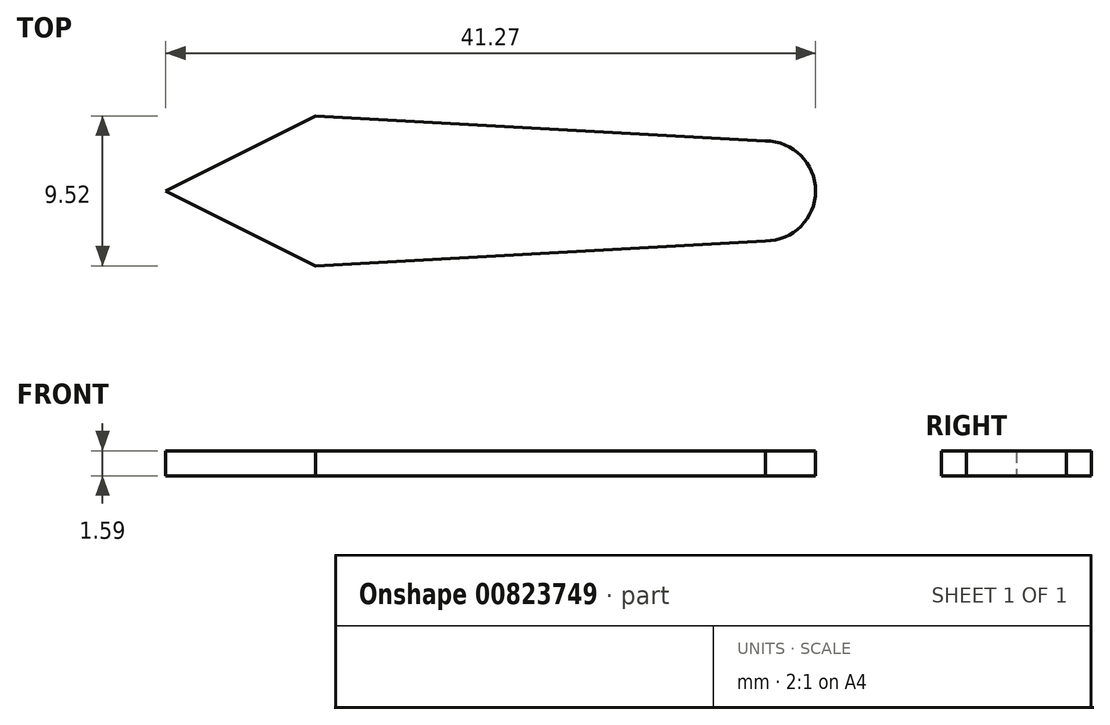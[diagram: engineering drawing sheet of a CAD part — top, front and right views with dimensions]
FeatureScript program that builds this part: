
annotation { "Feature Type Name" : "Feature", "Feature Type Description" : "" }
export const myFeature = defineFeature(function(context is Context, id is Id, definition is map)
    precondition{}
    {
        {
            var Q0;
            Q0=qCreatedBy(makeId("Top.planeOp"),FACE);
            var sketch = newSketch(context, id + "F0", { "sketchPlane" : qUnion([Q0])});
            skCircle(sketch, "E0", {"center": v(13.76, 0) * mm, "radius": 3.18 * mm});
            skLineSegment(sketch, "E1", {"start": v(13.76, 0) * mm, "end": v(-24.34, 0) * mm});
            skLineSegment(sketch, "E2", {"start": v(-24.34, 0) * mm, "end": v(-14.82, 4.76) * mm});
            skLineSegment(sketch, "E3", {"start": v(-14.82, 4.76) * mm, "end": v(13.76, 3.18) * mm});
            skLineSegment(sketch, "E4.MirrorCS", {"start": v(-24.34, 0) * mm, "end": v(-14.82, -4.76) * mm});
            skLineSegment(sketch, "E5.MirrorCS", {"start": v(-14.82, -4.76) * mm, "end": v(13.76, -3.17) * mm});
            skSolve(sketch);
        }
        {
            var Q0;
            {var subQ4=sQuery(id+"F0.wireOp",EDGE,"E2");Q0=makeQuery(id+"F0.imprint","IMPRINT",FACE,{"disambiguationData":[TD([[makeQuery(id+"F0.imprint","IMPRINT",EDGE,{"derivedFrom":subQ4}),-1.0]])]});}
            var Q1;
            {var subQ0=sQuery(id+"F0.wireOp",EDGE,"E0");var subQ1=makeQuery(id+"F0.imprint","INTERSECT",VERTEX,{"derivedFrom":[subQ0,sQuery(id+"F0.wireOp",EDGE,"E3")]});Q1=makeQuery(id+"F0.imprint","IMPRINT",FACE,{"disambiguationData":[TD([[makeQuery(id+"F0.imprint","IMPRINT",EDGE,{"disambiguationData":[TD([[subQ1,-1.0]])],"derivedFrom":subQ0}),1.0]])]});}
            var Q2;
            {var subQ4=sQuery(id+"F0.wireOp",EDGE,"E4.MirrorCS");Q2=makeQuery(id+"F0.imprint","IMPRINT",FACE,{"disambiguationData":[TD([[makeQuery(id+"F0.imprint","IMPRINT",EDGE,{"derivedFrom":subQ4}),1.0]])]});}
            extrude(context, id + "F1", {"entities" : qUnion([Q0, Q1, Q2]), "depth" : 1.59 * mm, "offsetDistance" : 25.4 * mm});
        }
    });
